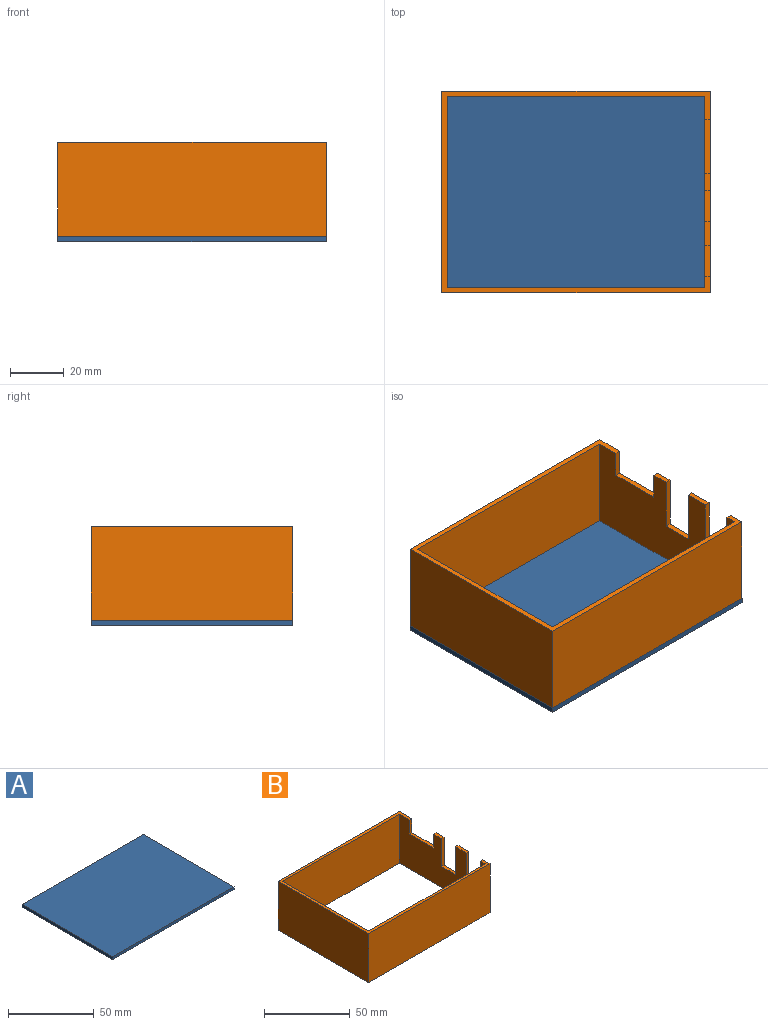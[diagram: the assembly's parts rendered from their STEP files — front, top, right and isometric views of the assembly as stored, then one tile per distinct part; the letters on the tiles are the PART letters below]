
ASSEMBLY  parts=2 mates=1
PART A: 6 faces, bbox 100x75x2 mm
  f0: plane 100x2mm, normal (0,1,0), area 200mm2, adj f1,f3,f4,f5
  f1: plane 75x2mm, normal (-1,0,0), area 150mm2, adj f0,f2,f4,f5
  f2: plane 100x2mm, normal (0,-1,0), area 200mm2, adj f1,f3,f4,f5
  f3: plane 75x2mm, normal (1,0,0), area 150mm2, adj f0,f2,f4,f5
  f4: plane 100x75mm, normal (0,0,1), area 7500mm2, adj f0,f1,f2,f3
  f5: plane 100x75mm, normal (0,0,-1), area 7500mm2, adj f0,f1,f2,f3
PART B: 21 faces, bbox 100x75x35 mm
  f0: plane 100x75mm, normal (0,0,1), area 566.9mm2, adj f1,f2,f5,f6,f7,f8,f9,f10
  f1: plane 71x35mm, normal (-1,0,0), area 1825.7mm2, adj f0,f3,f4,f9,f10,f11,f12,f13
  f2: plane 75x35mm, normal (1,0,0), area 1965.7mm2, adj f0,f3,f4,f5,f7,f11,f12,f13
  f3: plane 9.05x2mm, normal (0,0,1), area 18.1mm2, adj f1,f2,f13,f17
  f4: plane 6.58x2mm, normal (0,0,1), area 13.2mm2, adj f1,f2,f14,f18
  f5: plane 100x35mm, normal (0,1,0), area 3500mm2, adj f0,f2,f6,f11
  f6: plane 75x35mm, normal (-1,0,0), area 2625mm2, adj f0,f5,f7,f11
  f7: plane 100x35mm, normal (0,-1,0), area 3500mm2, adj f0,f2,f6,f11
  f8: plane 71x35mm, normal (1,0,0), area 2485mm2, adj f0,f9,f10,f11
  f9: plane 96x35mm, normal (0,-1,0), area 3360mm2, adj f0,f1,f8,f11
  f10: plane 96x35mm, normal (0,1,0), area 3360mm2, adj f0,f1,f8,f11
  f11: plane 100x75mm, normal (0,0,-1), area 684mm2, adj f1,f2,f5,f6,f7,f8,f9,f10
  f12: plane 11.47x2mm, normal (0,0,1), area 22.9mm2, adj f1,f2,f13,f14
  f13: plane 20.02x2mm, normal (0,1,0), area 40mm2, adj f1,f2,f3,f12
  f14: plane 20.02x2mm, normal (0,-1,0), area 40mm2, adj f1,f2,f4,f12
  f15: plane 11.47x2mm, normal (0,0,1), area 22.9mm2, adj f1,f2,f16,f17
  f16: plane 20.02x2mm, normal (0,1,0), area 40mm2, adj f0,f1,f2,f15
  f17: plane 20.02x2mm, normal (0,-1,0), area 40mm2, adj f1,f2,f3,f15
  f18: plane 10x2mm, normal (0,1,0), area 20mm2, adj f1,f2,f4,f19
  f19: plane 20x2mm, normal (0,0,1), area 40mm2, adj f1,f2,f18,f20
  f20: plane 10x2mm, normal (0,-1,0), area 20mm2, adj f0,f1,f2,f19
PLACE A t=(-29.61,18.27,4.47)mm
PLACE B rot(axis=(0.99,0.13,0.09),0deg) t=(-9.15,5.37,1.47)mm
MATE planar B.f11 <-> A.f4  axis (0,0,1) through (40.39,-35.73,1.47)mm
